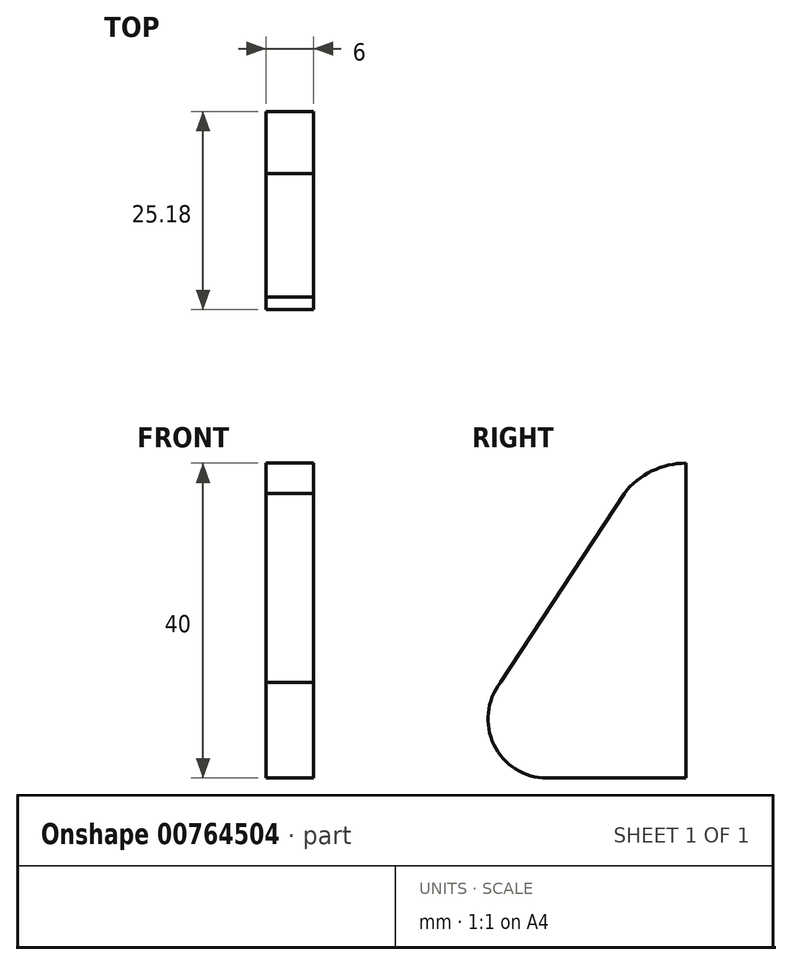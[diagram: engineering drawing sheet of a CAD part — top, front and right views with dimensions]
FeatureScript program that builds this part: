
annotation { "Feature Type Name" : "Feature", "Feature Type Description" : "" }
export const myFeature = defineFeature(function(context is Context, id is Id, definition is map)
    precondition{}
    {
        {
            var Q0;
            Q0=qCreatedBy(makeId("Right.planeOp"),FACE);
            var sketch = newSketch(context, id + "F0", { "sketchPlane" : qUnion([Q0])});
            skLineSegment(sketch, "E0.bottom", {"start": v(27.36, 43.18) * mm, "end": v(-7.64, 43.18) * mm});
            skLineSegment(sketch, "E0.top", {"start": v(27.36, -0.94) * mm, "end": v(-7.64, -0.94) * mm});
            skLineSegment(sketch, "E0.left", {"start": v(27.36, 43.18) * mm, "end": v(27.36, -0.94) * mm});
            skLineSegment(sketch, "E0.right", {"start": v(-7.64, 43.18) * mm, "end": v(-7.64, -0.94) * mm});
            skCircle(sketch, "E1", {"center": v(27.36, 33.18) * mm, "radius": 10 * mm});
            skCircle(sketch, "E2", {"center": v(2.36, -0.94) * mm, "radius": 10 * mm});
            skLineSegment(sketch, "E3", {"start": v(27.36, 33.18) * mm, "end": v(2.36, -0.94) * mm});
            skLineSegment(sketch, "E4", {"start": v(2.36, -0.94) * mm, "end": v(-5.7, 4.97) * mm});
            skLineSegment(sketch, "E5", {"start": v(27.36, 33.18) * mm, "end": v(19.3, 39.1) * mm});
            skLineSegment(sketch, "E6", {"start": v(19.3, 39.1) * mm, "end": v(-5.7, 4.97) * mm});
            skSolve(sketch);
        }
        {
            var Q0;
            {var subQ3=sQuery(id+"F0.wireOp",EDGE,"E5");Q0=makeQuery(id+"F0.imprint","IMPRINT",FACE,{"disambiguationData":[TD([[makeQuery(id+"F0.imprint","IMPRINT",EDGE,{"derivedFrom":subQ3}),-1.0]])]});}
            var Q1;
            {var subQ0=sQuery(id+"F0.wireOp",EDGE,"E5");Q1=makeQuery(id+"F0.imprint","IMPRINT",FACE,{"disambiguationData":[TD([[makeQuery(id+"F0.imprint","IMPRINT",EDGE,{"derivedFrom":subQ0}),1.0]])]});}
            var Q2;
            {var subQ1=sQuery(id+"F0.wireOp",EDGE,"E0.left");var subQ3=sQuery(id+"F0.wireOp",EDGE,"E1");var subQ4=makeQuery(id+"F0.imprint","INTERSECT",VERTEX,{"derivedFrom":[subQ1,subQ3]});Q2=makeQuery(id+"F0.imprint","IMPRINT",FACE,{"disambiguationData":[TD([[makeQuery(id+"F0.imprint","IMPRINT",EDGE,{"disambiguationData":[TD([[subQ4,1.0]])],"derivedFrom":subQ3}),1.0]])]});}
            var Q3;
            {var subQ1=sQuery(id+"F0.wireOp",EDGE,"E0.top");var subQ5=sQuery(id+"F0.wireOp",EDGE,"E0.left");var subQ6=makeQuery(id+"F0.imprint","INTERSECT",VERTEX,{"derivedFrom":[subQ1,subQ5]});Q3=makeQuery(id+"F0.imprint","IMPRINT",FACE,{"disambiguationData":[TD([[makeQuery(id+"F0.imprint","IMPRINT",EDGE,{"disambiguationData":[TD([[subQ6,-1.0]])],"derivedFrom":subQ1}),-1.0]])]});}
            var Q4;
            {var subQ0=sQuery(id+"F0.wireOp",EDGE,"E6");Q4=makeQuery(id+"F0.imprint","IMPRINT",FACE,{"disambiguationData":[TD([[makeQuery(id+"F0.imprint","IMPRINT",EDGE,{"derivedFrom":subQ0}),1.0]])]});}
            var Q5;
            {var subQ0=sQuery(id+"F0.wireOp",EDGE,"E4");Q5=makeQuery(id+"F0.imprint","IMPRINT",FACE,{"disambiguationData":[TD([[makeQuery(id+"F0.imprint","IMPRINT",EDGE,{"derivedFrom":subQ0}),-1.0]])]});}
            var Q6;
            {var subQ3=sQuery(id+"F0.wireOp",EDGE,"E4");Q6=makeQuery(id+"F0.imprint","IMPRINT",FACE,{"disambiguationData":[TD([[makeQuery(id+"F0.imprint","IMPRINT",EDGE,{"derivedFrom":subQ3}),1.0]])]});}
            var Q7;
            {var subQ1=sQuery(id+"F0.wireOp",EDGE,"E0.top");var subQ3=sQuery(id+"F0.wireOp",EDGE,"E2");var subQ4=makeQuery(id+"F0.imprint","INTERSECT",VERTEX,{"derivedFrom":[subQ1,subQ3]});Q7=makeQuery(id+"F0.imprint","IMPRINT",FACE,{"disambiguationData":[TD([[makeQuery(id+"F0.imprint","IMPRINT",EDGE,{"disambiguationData":[TD([[subQ4,-1.0]])],"derivedFrom":subQ3}),1.0]])]});}
            extrude(context, id + "F1", {"entities" : qUnion([Q0, Q1, Q2, Q3, Q4, Q5, Q6, Q7]), "depth" : (13 + 17.5) / 2 * mm, "offsetDistance" : 25 * mm});
        }
        {
            var Q0;
            Q0=makeQuery(id+"F1.opExtrude","SWEPT_EDGE",EDGE,{"disambiguationData":[OSD([sQuery(id+"F0.wireOp",EDGE,"E0.top"),sQuery(id+"F0.wireOp",EDGE,"E0.right"),sQuery(id+"F0.wireOp",EDGE,"E2")])]});
            fillet(context, id + "F2", {"entities" : qUnion([Q0]), "radius" : 10 * mm, "tangentPropagation" : true, "allowEdgeOverflow" : false});
        }
        {
            var Q0;
            Q0=makeQuery(id+"F1.opExtrude","CAP_FACE",FACE,{"disambiguationData":[OSD([sQuery(id+"F0.wireOp",EDGE,"E0.top"),sQuery(id+"F0.wireOp",EDGE,"E0.left"),sQuery(id+"F0.wireOp",EDGE,"E1"),sQuery(id+"F0.wireOp",EDGE,"E2"),sQuery(id+"F0.wireOp",EDGE,"E6")])],"isStart":false});
            var sketch = newSketch(context, id + "F3", { "sketchPlane" : qUnion([Q0])});
            skLineSegment(sketch, "E7.bottom", {"start": v(27.36, 6.56) * mm, "end": v(30.36, 6.56) * mm});
            skLineSegment(sketch, "E7.top", {"start": v(27.36, 2.56) * mm, "end": v(30.36, 2.56) * mm});
            skLineSegment(sketch, "E7.left", {"start": v(27.36, 6.56) * mm, "end": v(27.36, 2.56) * mm});
            skLineSegment(sketch, "E7.right", {"start": v(30.36, 6.56) * mm, "end": v(30.36, 2.56) * mm});
            skLineSegment(sketch, "E8.bottom", {"start": v(30.36, 6.56) * mm, "end": v(33.36, 6.56) * mm});
            skLineSegment(sketch, "E8.top", {"start": v(30.36, 2.06) * mm, "end": v(33.36, 2.06) * mm});
            skLineSegment(sketch, "E8.left", {"start": v(30.36, 6.56) * mm, "end": v(30.36, 2.06) * mm});
            skLineSegment(sketch, "E8.right", {"start": v(33.36, 6.56) * mm, "end": v(33.36, 2.06) * mm});
            skSolve(sketch);
        }
        {
            var Q0;
            {var subQ0=sQuery(id+"F3.wireOp",EDGE,"E7.bottom");Q0=makeQuery(id+"F3.imprint","IMPRINT",FACE,{"disambiguationData":[TD([[makeQuery(id+"F3.imprint","IMPRINT",EDGE,{"derivedFrom":subQ0}),-1.0]])]});}
            var Q1;
            {var subQ3=sQuery(id+"F3.wireOp",EDGE,"E8.bottom");Q1=makeQuery(id+"F3.imprint","IMPRINT",FACE,{"disambiguationData":[TD([[makeQuery(id+"F3.imprint","IMPRINT",EDGE,{"derivedFrom":subQ3}),-1.0]])]});}
            var Q2;
            Q2=sQuery(id+"F3.wireOp",EDGE,"E7.bottom");
            revolve(context, id + "F4", {"operationType" : NewBodyOperationType.ADD, "surfaceOperationType" : NewSurfaceOperationType.NEW, "entities" : qUnion([Q0, Q1]), "axis" : qUnion([Q2]), "revolveType" : RevolveType.ONE_DIRECTION, "angle" : 180 * degree});
        }
        {
            var Q0;
            Q0=makeQuery(id+"F1.opExtrude","SWEPT_BODY",BODY,{"disambiguationData":[OSD([sQuery(id+"F0.wireOp",EDGE,"E0.top"),sQuery(id+"F0.wireOp",EDGE,"E0.left"),sQuery(id+"F0.wireOp",EDGE,"E1"),sQuery(id+"F0.wireOp",EDGE,"E2"),sQuery(id+"F0.wireOp",EDGE,"E6")])]});
            var Q1;
            Q1=makeQuery(id+"F4.boolean.opBoolean","MERGE",FACE,{"derivedFrom":[makeQuery(id+"F1.opExtrude","CAP_FACE",FACE,{"disambiguationData":[OSD([sQuery(id+"F0.wireOp",EDGE,"E0.top"),sQuery(id+"F0.wireOp",EDGE,"E0.left"),sQuery(id+"F0.wireOp",EDGE,"E1"),sQuery(id+"F0.wireOp",EDGE,"E2"),sQuery(id+"F0.wireOp",EDGE,"E6")])],"isStart":false}),makeQuery(id+"F4.opRevolve","CAP_FACE",FACE,{"disambiguationData":[OSD([sQuery(id+"F3.wireOp",EDGE,"E7.bottom"),sQuery(id+"F3.wireOp",EDGE,"E7.top"),sQuery(id+"F3.wireOp",EDGE,"E7.left"),sQuery(id+"F3.wireOp",EDGE,"E8.bottom"),sQuery(id+"F3.wireOp",EDGE,"E8.top"),sQuery(id+"F3.wireOp",EDGE,"E8.left"),sQuery(id+"F3.wireOp",EDGE,"E8.right")])],"isStart":false})]});
            mirror(context, id + "F5", {"entities" : qUnion([Q0]), "mirrorPlane" : qUnion([Q1])});
        }
        {
            var Q0;
            Q0=makeQuery(id+"F1.opExtrude","SWEPT_BODY",BODY,{"disambiguationData":[OSD([sQuery(id+"F0.wireOp",EDGE,"E0.top"),sQuery(id+"F0.wireOp",EDGE,"E0.left"),sQuery(id+"F0.wireOp",EDGE,"E1"),sQuery(id+"F0.wireOp",EDGE,"E2"),sQuery(id+"F0.wireOp",EDGE,"E6")])]});
            deleteBodies(context, id + "F6", {"entities" : qUnion([Q0])});
        }
        {
            var Q0;
            Q0=makeQuery(id+"F5.opPattern","COPY",FACE,{"derivedFrom":makeQuery(id+"F1.opExtrude","CAP_FACE",FACE,{"disambiguationData":[OSD([sQuery(id+"F0.wireOp",EDGE,"E0.top"),sQuery(id+"F0.wireOp",EDGE,"E0.left"),sQuery(id+"F0.wireOp",EDGE,"E1"),sQuery(id+"F0.wireOp",EDGE,"E2"),sQuery(id+"F0.wireOp",EDGE,"E6")])],"isStart":true}),"instanceName":"1"});
            var sketch = newSketch(context, id + "F7", { "sketchPlane" : qUnion([Q0])});
            skLineSegment(sketch, "E9.bottom", {"start": v(9.68, -0.94) * mm, "end": v(27.36, -0.94) * mm});
            skLineSegment(sketch, "E9.top", {"start": v(9.68, 14.06) * mm, "end": v(27.36, 14.06) * mm});
            skLineSegment(sketch, "E9.left", {"start": v(9.68, -0.94) * mm, "end": v(9.68, 14.06) * mm});
            skLineSegment(sketch, "E9.right", {"start": v(27.36, -0.94) * mm, "end": v(27.36, 14.06) * mm});
            skCircle(sketch, "E10", {"center": v(9.68, 6.56) * mm, "radius": 7.5 * mm});
            skCircle(sketch, "E11", {"center": v(27.36, 29.06) * mm, "radius": 10 * mm});
            skLineSegment(sketch, "E12", {"start": v(27.36, 29.06) * mm, "end": v(9.68, 6.56) * mm});
            skLineSegment(sketch, "E13", {"start": v(27.36, 29.06) * mm, "end": v(19.5, 35.24) * mm});
            skLineSegment(sketch, "E14", {"start": v(9.68, 6.56) * mm, "end": v(3.79, 11.2) * mm});
            skLineSegment(sketch, "E15", {"start": v(3.79, 11.2) * mm, "end": v(19.5, 35.24) * mm});
            skSolve(sketch);
        }
        {
            var Q0;
            {var subQ0=sQuery(id+"F7.wireOp",EDGE,"E13");Q0=makeQuery(id+"F7.imprint","IMPRINT",FACE,{"disambiguationData":[TD([[makeQuery(id+"F7.imprint","IMPRINT",EDGE,{"derivedFrom":subQ0}),-1.0]])]});}
            var Q1;
            {var subQ0=sQuery(id+"F7.wireOp",EDGE,"E13");Q1=makeQuery(id+"F7.imprint","IMPRINT",FACE,{"disambiguationData":[TD([[makeQuery(id+"F7.imprint","IMPRINT",EDGE,{"derivedFrom":subQ0}),1.0]])]});}
            var Q2;
            {var subQ0=sQuery(id+"F7.wireOp",EDGE,"E12");var subQ1=sQuery(id+"F7.wireOp",EDGE,"E11");var subQ2=makeQuery(id+"F7.imprint","INTERSECT",VERTEX,{"derivedFrom":[subQ1,subQ0]});Q2=makeQuery(id+"F7.imprint","IMPRINT",FACE,{"disambiguationData":[TD([[makeQuery(id+"F7.imprint","IMPRINT",EDGE,{"disambiguationData":[TD([[subQ2,-1.0]])],"derivedFrom":subQ1}),1.0]])]});}
            var Q3;
            {var subQ7=sQuery(id+"F7.wireOp",EDGE,"E15");Q3=makeQuery(id+"F7.imprint","IMPRINT",FACE,{"disambiguationData":[TD([[makeQuery(id+"F7.imprint","IMPRINT",EDGE,{"derivedFrom":subQ7}),-1.0]])]});}
            var Q4;
            {var subQ0=sQuery(id+"F7.wireOp",EDGE,"E10");var subQ3=sQuery(id+"F7.wireOp",EDGE,"E12");var subQ5=makeQuery(id+"F7.imprint","INTERSECT",VERTEX,{"derivedFrom":[subQ0,subQ3]});Q4=makeQuery(id+"F7.imprint","IMPRINT",FACE,{"disambiguationData":[TD([[makeQuery(id+"F7.imprint","IMPRINT",EDGE,{"disambiguationData":[TD([[subQ5,-1.0]])],"derivedFrom":subQ0}),1.0]])]});}
            var Q5;
            {var subQ3=sQuery(id+"F7.wireOp",EDGE,"E14");Q5=makeQuery(id+"F7.imprint","IMPRINT",FACE,{"disambiguationData":[TD([[makeQuery(id+"F7.imprint","IMPRINT",EDGE,{"derivedFrom":subQ3}),-1.0]])]});}
            var Q6;
            {var subQ5=sQuery(id+"F7.wireOp",EDGE,"E14");Q6=makeQuery(id+"F7.imprint","IMPRINT",FACE,{"disambiguationData":[TD([[makeQuery(id+"F7.imprint","IMPRINT",EDGE,{"derivedFrom":subQ5}),1.0]])]});}
            var Q7;
            {var subQ0=sQuery(id+"F7.wireOp",EDGE,"E10");var subQ5=sQuery(id+"F7.wireOp",EDGE,"E12");var subQ7=makeQuery(id+"F7.imprint","INTERSECT",VERTEX,{"derivedFrom":[subQ0,subQ5]});Q7=makeQuery(id+"F7.imprint","IMPRINT",FACE,{"disambiguationData":[TD([[makeQuery(id+"F7.imprint","IMPRINT",EDGE,{"disambiguationData":[TD([[subQ7,-1.0]])],"derivedFrom":subQ5}),1.0]])]});}
            var Q8;
            {var subQ1=sQuery(id+"F7.wireOp",EDGE,"E9.bottom");Q8=makeQuery(id+"F7.imprint","IMPRINT",FACE,{"disambiguationData":[TD([[makeQuery(id+"F7.imprint","IMPRINT",EDGE,{"derivedFrom":subQ1}),-1.0]])]});}
            var Q9;
            {var subQ3=sQuery(id+"F7.wireOp",EDGE,"E12");var subQ5=sQuery(id+"F7.wireOp",EDGE,"E11");var subQ6=makeQuery(id+"F7.imprint","INTERSECT",VERTEX,{"derivedFrom":[subQ5,subQ3]});Q9=makeQuery(id+"F7.imprint","IMPRINT",FACE,{"disambiguationData":[TD([[makeQuery(id+"F7.imprint","IMPRINT",EDGE,{"disambiguationData":[TD([[subQ6,-1.0]])],"derivedFrom":subQ5}),-1.0]])]});}
            var Q10;
            {var subQ1=sQuery(id+"F7.wireOp",EDGE,"E9.top");var subQ3=sQuery(id+"F7.wireOp",EDGE,"E12");var subQ4=makeQuery(id+"F7.imprint","INTERSECT",VERTEX,{"derivedFrom":[subQ1,subQ3]});Q10=makeQuery(id+"F7.imprint","IMPRINT",FACE,{"disambiguationData":[TD([[makeQuery(id+"F7.imprint","IMPRINT",EDGE,{"disambiguationData":[TD([[subQ4,-1.0]])],"derivedFrom":subQ3}),-1.0]])]});}
            var Q11;
            {var subQ0=sQuery(id+"F7.wireOp",EDGE,"E15");var subQ1=sQuery(id+"F7.wireOp",EDGE,"E11");var subQ2=makeQuery(id+"F7.imprint","INTERSECT",VERTEX,{"derivedFrom":[subQ1,subQ0]});Q11=makeQuery(id+"F7.imprint","IMPRINT",FACE,{"disambiguationData":[TD([[makeQuery(id+"F7.imprint","IMPRINT",EDGE,{"disambiguationData":[TD([[subQ2,-1.0]])],"derivedFrom":subQ1}),-1.0]])]});}
            extrude(context, id + "F8", {"entities" : qUnion([Q0, Q1, Q2, Q3, Q4, Q5, Q6, Q7, Q8, Q9, Q10, Q11]), "depth" : 6 * mm, "offsetDistance" : 25 * mm});
        }
        {
            var Q0;
            Q0=makeQuery(id+"F5.opPattern","COPY",BODY,{"derivedFrom":makeQuery(id+"F1.opExtrude","SWEPT_BODY",BODY,{"disambiguationData":[OSD([sQuery(id+"F0.wireOp",EDGE,"E0.top"),sQuery(id+"F0.wireOp",EDGE,"E0.left"),sQuery(id+"F0.wireOp",EDGE,"E1"),sQuery(id+"F0.wireOp",EDGE,"E2"),sQuery(id+"F0.wireOp",EDGE,"E6")])]}),"instanceName":"1"});
            deleteBodies(context, id + "F9", {"entities" : qUnion([Q0])});
        }
    });
